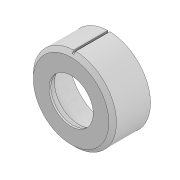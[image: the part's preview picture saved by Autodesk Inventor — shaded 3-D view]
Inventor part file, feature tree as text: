
AUTODESK INVENTOR PART (.ipt)
format: ipt  version: 2021 (Build 250183000, 183)  size: 125,440 bytes
history: native  units: mm
features: extrude x4, sketch x2, chamfer x1
ambient origin geometry x8: Origin, YZ Plane, XZ Plane, XY Plane, X Axis, Y Axis, Z Axis, Center Point
bodies: Solid1 (feature_tree)
feature tree (7):
  sketch  "Sketch1"  dims[d0=42.2mm d1=44.0mm]
  extrude  "Extrusion1"  Depth=44.0mm
  extrude  "Extrusion2"  Depth=1.0mm
  extrude  "Extrusion3"  Depth=1.0mm TaperAngle=0.0deg
  chamfer  "Chamfer1"  Distance=20.0mm
  extrude  "Extrusion4"  Depth=1.0mm TaperAngle=0.0deg
  sketch  "Sketch2"  dims[d2=25.6mm d3=23.4mm d4=4.0mm d5=0.0mm d6=20.0mm d7=0.0mm d8=1.0mm d9=0.0mm d10=2.0mm d11=2.0mm d12=45.0deg d13=1.0mm d15=1.0mm d16=2.0mm d17=20.0mm d18=0.0mm]
